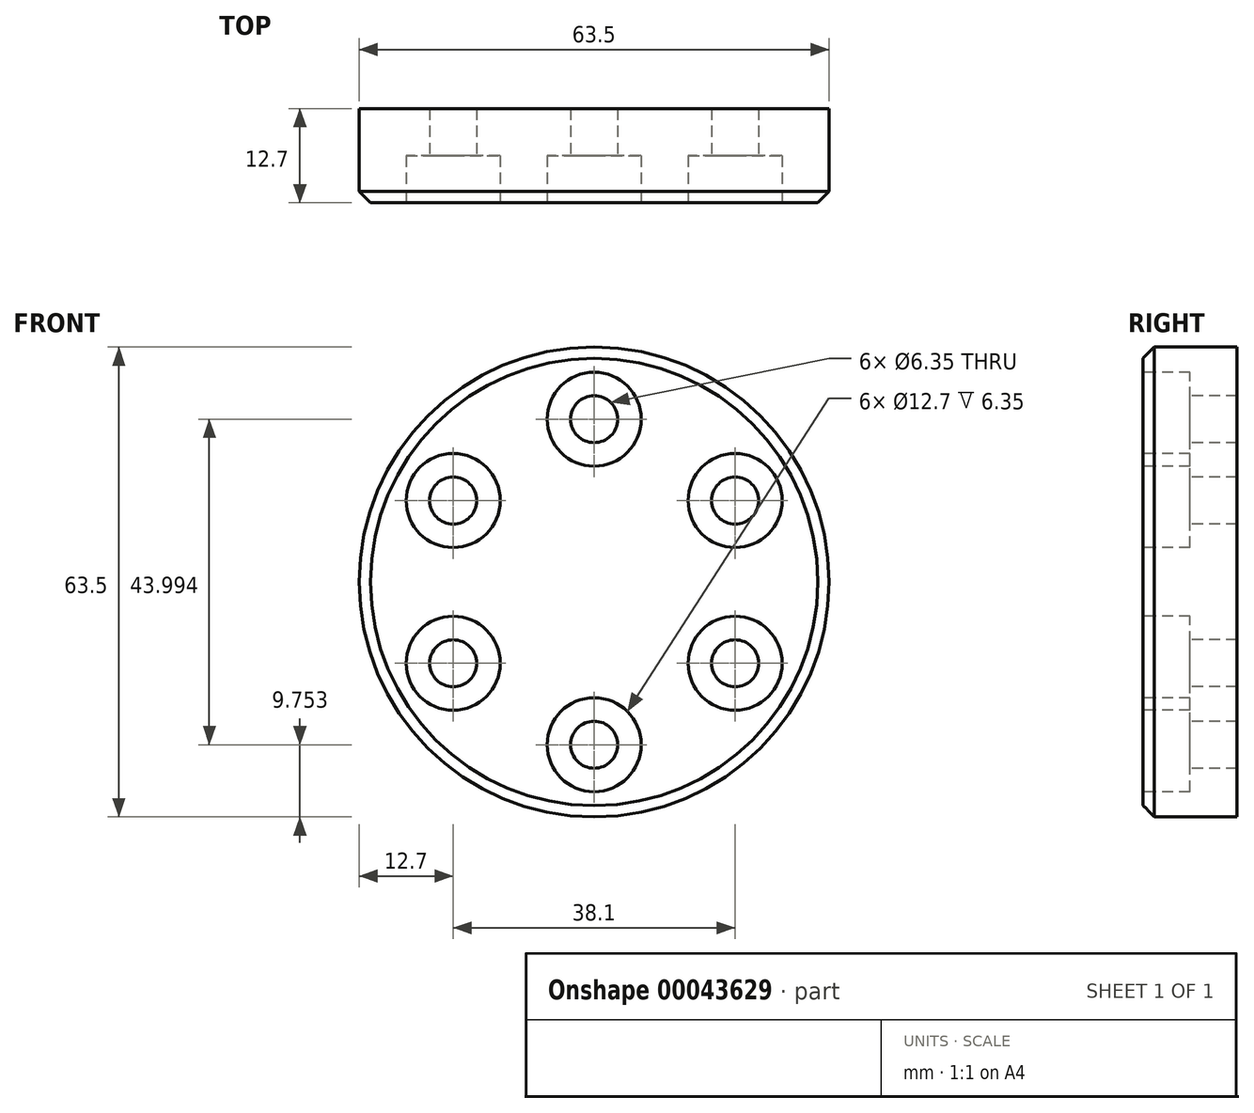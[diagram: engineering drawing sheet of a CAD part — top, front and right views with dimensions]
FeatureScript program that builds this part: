
annotation { "Feature Type Name" : "Feature", "Feature Type Description" : "" }
export const myFeature = defineFeature(function(context is Context, id is Id, definition is map)
    precondition{}
    {
        {
            var Q0;
            Q0=qCreatedBy(makeId("Front.planeOp"),FACE);
            var sketch = newSketch(context, id + "F0", { "sketchPlane" : qUnion([Q0])});
            skCircle(sketch, "E0", {"center": v(0, 0) * mm, "radius": 31.75 * mm});
            skSolve(sketch);
        }
        {
            var Q0;
            Q0 = qSketchRegion(id + "F0", true);
            extrude(context, id + "F1", {"entities" : qUnion([Q0]), "endBound" : BoundingType.SYMMETRIC, "depth" : 12.7 * mm});
        }
        {
            var Q0;
            Q0=makeQuery(id+"F1.opExtrude","CAP_FACE",FACE,{"disambiguationData":[OSD([sQuery(id+"F0.wireOp",EDGE,"E0")])],"isStart":false});
            var sketch = newSketch(context, id + "F2", { "sketchPlane" : qUnion([Q0])});
            skCircle(sketch, "E1.cCircle", {"center": v(0, 0) * mm, "radius": 19.05 * mm, "construction": true});
            skLineSegment(sketch, "E1.0", {"start": v(19.05, -11) * mm, "end": v(0, -22) * mm});
            skLineSegment(sketch, "E1.1", {"start": v(0, -22) * mm, "end": v(-19.05, -11) * mm});
            skLineSegment(sketch, "E1.2", {"start": v(-19.05, -11) * mm, "end": v(-19.05, 11) * mm});
            skLineSegment(sketch, "E1.3", {"start": v(-19.05, 11) * mm, "end": v(0, 22) * mm});
            skLineSegment(sketch, "E1.4", {"start": v(0, 22) * mm, "end": v(19.05, 11) * mm});
            skLineSegment(sketch, "E1.5", {"start": v(19.05, 11) * mm, "end": v(19.05, -11) * mm});
            skSolve(sketch);
        }
        {
            var Q0;
            Q0=sQuery(id+"F2.wireOp",VERTEX,"E1.3.start");
            var Q1;
            Q1=sQuery(id+"F2.wireOp",VERTEX,"E1.4.start");
            var Q2;
            Q2=sQuery(id+"F2.wireOp",VERTEX,"E1.5.start");
            var Q3;
            Q3=sQuery(id+"F2.wireOp",VERTEX,"E1.0.start");
            var Q4;
            Q4=sQuery(id+"F2.wireOp",VERTEX,"E1.1.start");
            var Q5;
            Q5=sQuery(id+"F2.wireOp",VERTEX,"E1.2.start");
            var Q6;
            Q6=makeQuery(id+"F1.opExtrude","SWEPT_BODY",BODY,{"disambiguationData":[OSD([sQuery(id+"F0.wireOp",EDGE,"E0")])]});
            hole(context, id + "F3", {"style" : HoleStyle.C_BORE, "holeDiameter" : 6.35 * mm, "cBoreDiameter" : 12.7 * mm, "cBoreDepth" : 6.35 * mm, "endStyle" : HoleEndStyle.THROUGH, "locations" : qUnion([Q0, Q1, Q2, Q3, Q4, Q5]), "scope" : qUnion([Q6])});
        }
        {
            var Q0;
            Q0=makeQuery(id+"F1.opExtrude","CAP_EDGE",EDGE,{"disambiguationData":[OSD([sQuery(id+"F0.wireOp",EDGE,"E0")])],"isStart":false});
            chamfer(context, id + "F4", {"entities" : qUnion([Q0]), "width" : 1.52 * mm, "tangentPropagation" : true});
        }
    });
